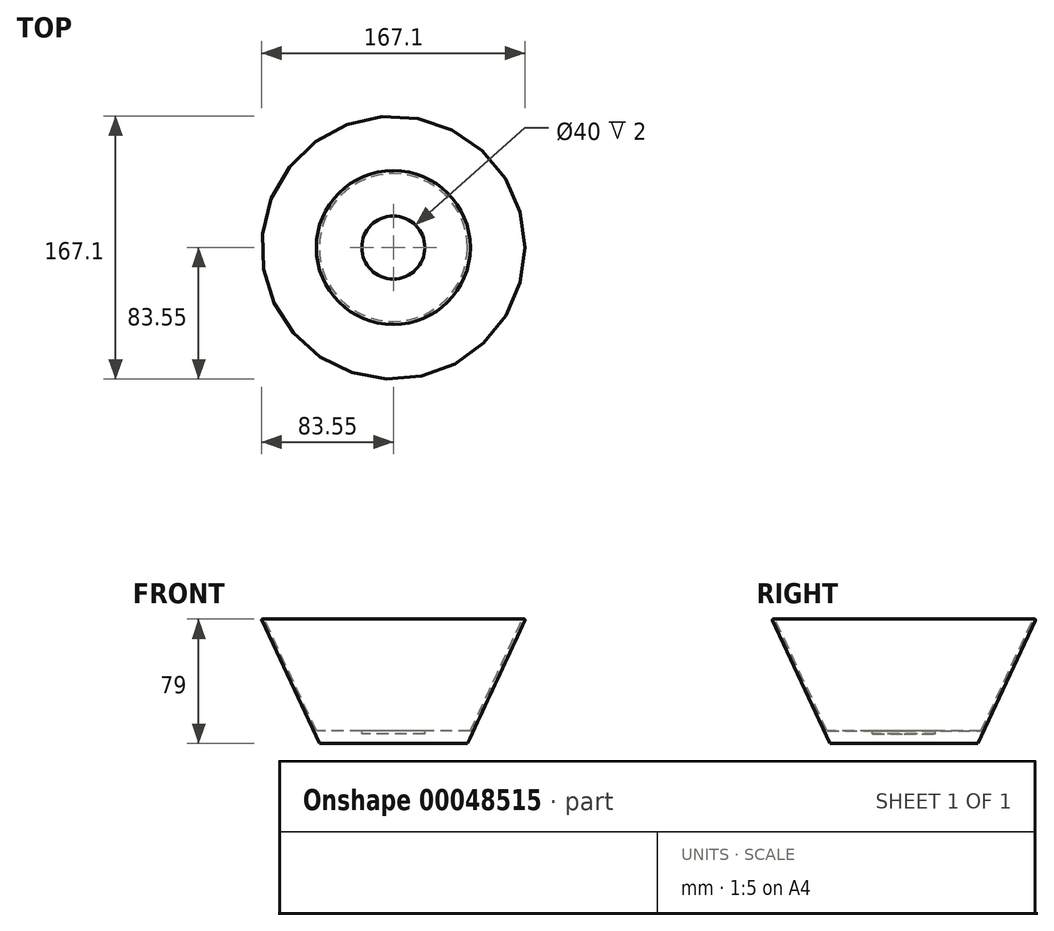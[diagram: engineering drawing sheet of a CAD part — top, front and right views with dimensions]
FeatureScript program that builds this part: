
annotation { "Feature Type Name" : "Feature", "Feature Type Description" : "" }
export const myFeature = defineFeature(function(context is Context, id is Id, definition is map)
    precondition{}
    {
        {
            var Q0;
            Q0=qCreatedBy(makeId("Top.planeOp"),FACE);
            var sketch = newSketch(context, id + "F0", { "sketchPlane" : qUnion([Q0])});
            skCircle(sketch, "E0", {"center": v(0, 0) * mm, "radius": 47 * mm});
            skSolve(sketch);
        }
        {
            var Q0;
            Q0=makeQuery(id+"F0.imprint","IMPRINT",FACE,{"disambiguationData":[TD([[makeQuery(id+"F0.imprint","IMPRINT",EDGE,{"derivedFrom":sQuery(id+"F0.wireOp",EDGE,"E0")}),1.0]])]});
            extrude(context, id + "F1", {"entities" : qUnion([Q0]), "depth" : 79 * mm, "hasDraft" : true, "draftAngle" : 25 * degree});
        }
        {
            var Q0;
            Q0=makeQuery(id+"F1.opExtrude","CAP_FACE",FACE,{"disambiguationData":[OSD([sQuery(id+"F0.wireOp",EDGE,"E0")])],"isStart":false});
            var sketch = newSketch(context, id + "F2", { "sketchPlane" : qUnion([Q0])});
            skCircle(sketch, "E1", {"center": v(0, 0) * mm, "radius": 82 * mm});
            skSolve(sketch);
        }
        {
            var Q0;
            Q0=makeQuery(id+"F2.imprint","IMPRINT",FACE,{"disambiguationData":[TD([[makeQuery(id+"F2.imprint","IMPRINT",EDGE,{"derivedFrom":sQuery(id+"F2.wireOp",EDGE,"E1")}),1.0]])]});
            var Q1;
            Q1=sQuery(id+"F2.wireOp",EDGE,"E1");
            extrude(context, id + "F3", {"entities" : qUnion([Q0]), "operationType" : NewBodyOperationType.REMOVE, "surfaceEntities" : qUnion([Q1]), "oppositeDirection" : true, "depth" : 71 * mm, "hasDraft" : true, "draftAngle" : 25 * degree, "draftPullDirection" : true});
        }
        {
            var Q0;
            Q0=makeQuery(id+"F3.boolean.opBoolean","COPY",FACE,{"derivedFrom":makeQuery(id+"F3.opExtrude","CAP_FACE",FACE,{"disambiguationData":[OSD([sQuery(id+"F2.wireOp",EDGE,"E1")])],"isStart":false})});
            var sketch = newSketch(context, id + "F4", { "sketchPlane" : qUnion([Q0])});
            skCircle(sketch, "E2", {"center": v(0, 0) * mm, "radius": 20 * mm});
            skSolve(sketch);
        }
        {
            var Q0;
            Q0=makeQuery(id+"F4.imprint","IMPRINT",FACE,{"disambiguationData":[TD([[makeQuery(id+"F4.imprint","IMPRINT",EDGE,{"derivedFrom":sQuery(id+"F4.wireOp",EDGE,"E2")}),1.0]])]});
            var Q1;
            Q1=sQuery(id+"F4.wireOp",EDGE,"E2");
            extrude(context, id + "F5", {"entities" : qUnion([Q0]), "operationType" : NewBodyOperationType.REMOVE, "surfaceEntities" : qUnion([Q1]), "oppositeDirection" : true, "depth" : 2 * mm});
        }
        {
            var Q0;
            Q0=makeQuery(id+"F1.opExtrude","CAP_FACE",FACE,{"disambiguationData":[OSD([sQuery(id+"F0.wireOp",EDGE,"E0")])],"isStart":false});
            fillet(context, id + "F6", {"entities" : qUnion([Q0]), "radius" : 0.5 * mm, "tangentPropagation" : true, "allowEdgeOverflow" : false});
        }
    });
